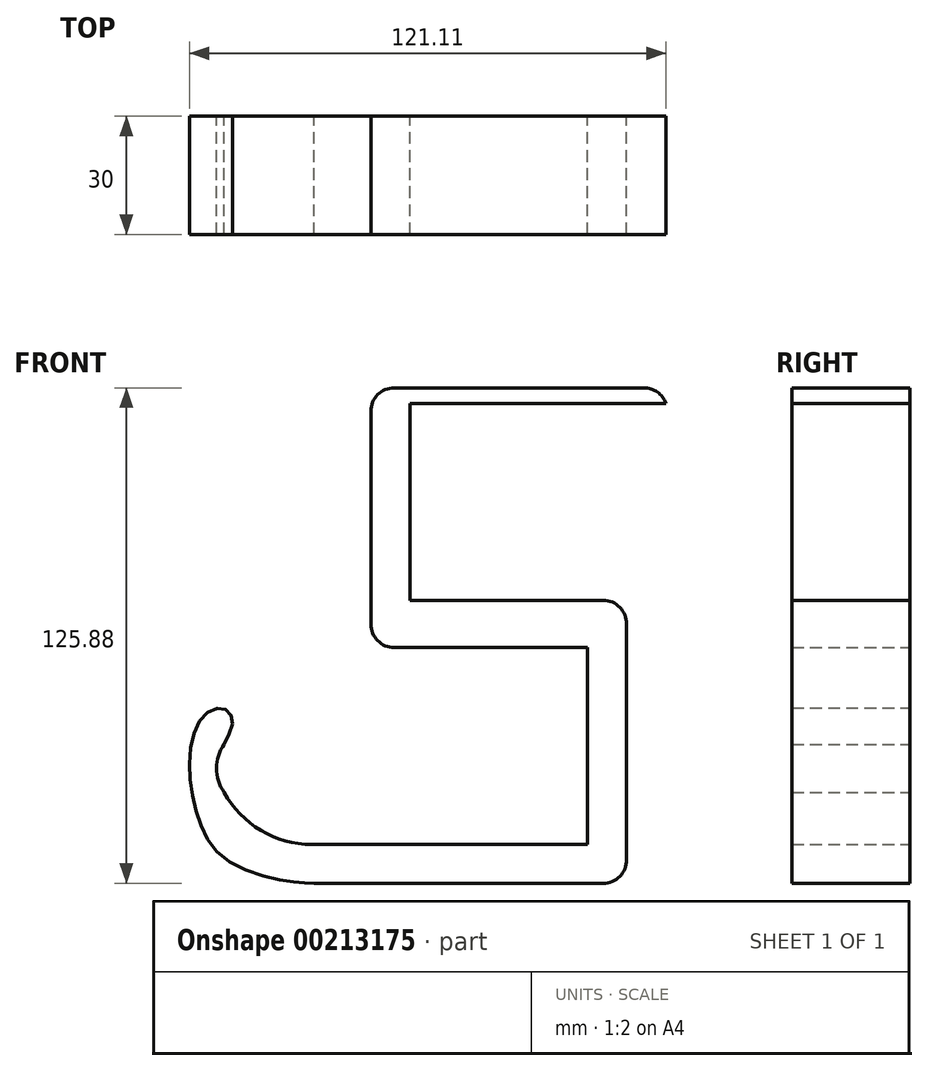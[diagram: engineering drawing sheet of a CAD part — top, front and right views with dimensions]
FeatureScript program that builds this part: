
annotation { "Feature Type Name" : "Feature", "Feature Type Description" : "" }
export const myFeature = defineFeature(function(context is Context, id is Id, definition is map)
    precondition{}
    {
        {
            var Q0;
            Q0=qCreatedBy(makeId("Front.planeOp"),FACE);
            var sketch = newSketch(context, id + "F0", { "sketchPlane" : qUnion([Q0])});
            skLineSegment(sketch, "E0", {"start": v(44.54, 41.8) * mm, "end": v(-20.46, 41.8) * mm});
            skLineSegment(sketch, "E1", {"start": v(44.54, 41.8) * mm, "end": v(44.54, 45.8) * mm});
            skLineSegment(sketch, "E2", {"start": v(44.54, 45.8) * mm, "end": v(-30.46, 45.8) * mm});
            skLineSegment(sketch, "E3", {"start": v(-20.46, 41.8) * mm, "end": v(-20.46, -8.2) * mm});
            skLineSegment(sketch, "E4", {"start": v(-20.46, -8.2) * mm, "end": v(34.54, -8.2) * mm});
            skLineSegment(sketch, "E5", {"start": v(-30.46, 45.8) * mm, "end": v(-30.46, -20.2) * mm});
            skLineSegment(sketch, "E6", {"start": v(-30.46, -20.2) * mm, "end": v(24.54, -20.2) * mm});
            skLineSegment(sketch, "E7", {"start": v(24.54, -20.2) * mm, "end": v(24.54, -70.2) * mm});
            skLineSegment(sketch, "E8", {"start": v(24.54, -70.2) * mm, "end": v(-45.46, -70.2) * mm});
            skArc(sketch, "E9", {"start": v(-67.74, -56.98) * mm, "mid": v(-58.41, -66.65) * mm, "end": v(-45.46, -70.2) * mm});
            skArc(sketch, "E10", {"start": v(-67.74, -44.76) * mm, "mid": v(-69.67, -50.87) * mm, "end": v(-67.74, -56.98) * mm});
            skFitSpline(sketch, "E11", {"points": [v(-67.74, -44.76) * mm, v(-65.61, -38.66) * mm, v(-67.74, -35.74) * mm, v(-72.78, -37.33) * mm, v(-76.5, -47.95) * mm, v(-74.64, -62.3) * mm, v(-67.74, -73.71) * mm, v(-51.54, -79.55) * mm, v(-44.9, -80.08) * mm], "startDerivative": vector(32.42, 61.62) * mm, "endDerivative": vector(53.18, -1.1) * mm});
            skLineSegment(sketch, "E12", {"start": v(-44.9, -80.08) * mm, "end": v(34.54, -80.08) * mm});
            skLineSegment(sketch, "E13", {"start": v(34.54, -8.2) * mm, "end": v(34.54, -80.08) * mm});
            skSolve(sketch);
        }
        {
            var Q0;
            Q0=makeQuery(id+"F0.imprint","IMPRINT",FACE,{"disambiguationData":[TD([[makeQuery(id+"F0.imprint","IMPRINT",EDGE,{"derivedFrom":sQuery(id+"F0.wireOp",EDGE,"E0")}),-1.0]])]});
            extrude(context, id + "F1", {"entities" : qUnion([Q0]), "depth" : 30 * mm});
        }
        {
            var Q0;
            Q0=makeQuery(id+"F1.opExtrude","SWEPT_EDGE",EDGE,{"disambiguationData":[OSD([sQuery(id+"F0.wireOp",EDGE,"E2"),sQuery(id+"F0.wireOp",EDGE,"E5")])]});
            var Q1;
            Q1=makeQuery(id+"F1.opExtrude","SWEPT_EDGE",EDGE,{"disambiguationData":[OSD([sQuery(id+"F0.wireOp",EDGE,"E5"),sQuery(id+"F0.wireOp",EDGE,"E6")])]});
            var Q2;
            Q2=makeQuery(id+"F1.opExtrude","SWEPT_EDGE",EDGE,{"disambiguationData":[OSD([sQuery(id+"F0.wireOp",EDGE,"E4"),sQuery(id+"F0.wireOp",EDGE,"E13")])]});
            var Q3;
            Q3=makeQuery(id+"F1.opExtrude","SWEPT_EDGE",EDGE,{"disambiguationData":[OSD([sQuery(id+"F0.wireOp",EDGE,"E12"),sQuery(id+"F0.wireOp",EDGE,"E13")])]});
            var Q4;
            Q4=makeQuery(id+"F1.opExtrude","SWEPT_EDGE",EDGE,{"disambiguationData":[OSD([sQuery(id+"F0.wireOp",EDGE,"E1"),sQuery(id+"F0.wireOp",EDGE,"E2")])]});
            fillet(context, id + "F2", {"entities" : qUnion([Q0, Q1, Q2, Q3, Q4]), "radius" : 6 * mm, "tangentPropagation" : true, "allowEdgeOverflow" : false});
        }
    });
